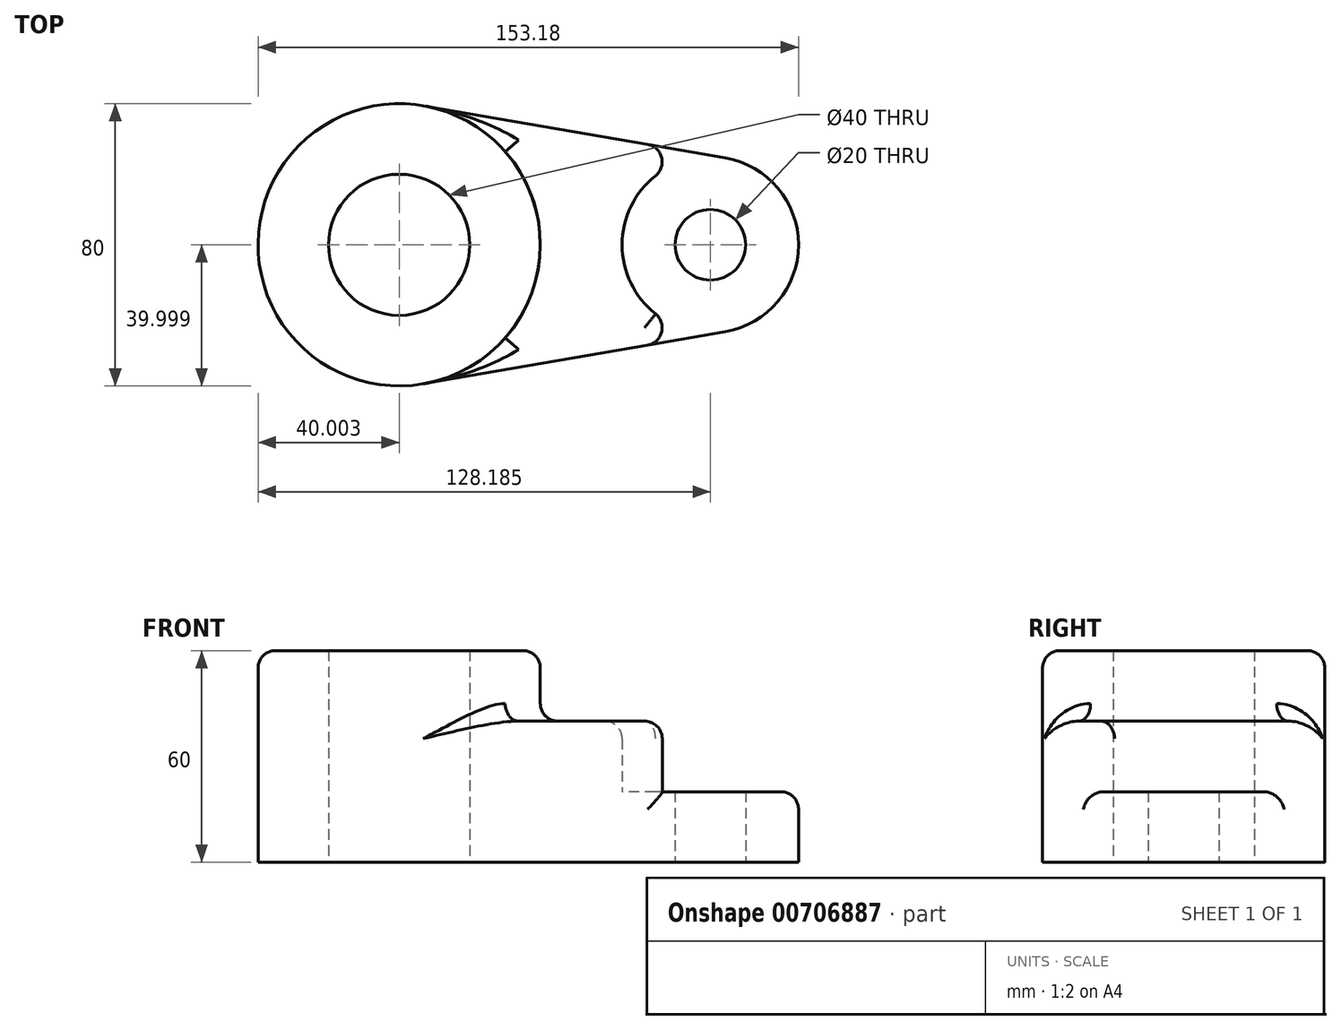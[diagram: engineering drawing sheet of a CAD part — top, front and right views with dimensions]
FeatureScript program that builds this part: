
annotation { "Feature Type Name" : "Feature", "Feature Type Description" : "" }
export const myFeature = defineFeature(function(context is Context, id is Id, definition is map)
    precondition{}
    {
        {
            var Q0;
            Q0=qCreatedBy(makeId("Top.planeOp"),FACE);
            var sketch = newSketch(context, id + "F0", { "sketchPlane" : qUnion([Q0])});
            skCircle(sketch, "E0", {"center": v(-39.4, 19.58) * mm, "radius": 40 * mm});
            skCircle(sketch, "E1", {"center": v(-39.4, 19.58) * mm, "radius": 20 * mm});
            skCircle(sketch, "E2", {"center": v(48.77, 19.58) * mm, "radius": 10 * mm});
            skCircle(sketch, "E3", {"center": v(48.77, 19.58) * mm, "radius": 25 * mm});
            skLineSegment(sketch, "E4", {"start": v(-32.6, 59) * mm, "end": v(53.03, 44.21) * mm});
            skLineSegment(sketch, "E5", {"start": v(-32.6, -19.84) * mm, "end": v(53.03, -5.06) * mm});
            skSolve(sketch);
        }
        {
            var Q0;
            Q0=makeQuery(id+"F0.imprint","IMPRINT",FACE,{"disambiguationData":[TD([[makeQuery(id+"F0.imprint","IMPRINT",EDGE,{"derivedFrom":sQuery(id+"F0.wireOp",EDGE,"E1")}),-1.0]])]});
            extrude(context, id + "F1", {"entities" : qUnion([Q0]), "depth" : 60 * mm, "offsetDistance" : 25 * mm});
        }
        {
            var Q0;
            {var subQ0=sQuery(id+"F0.wireOp",EDGE,"E4");Q0=makeQuery(id+"F0.imprint","IMPRINT",FACE,{"disambiguationData":[TD([[makeQuery(id+"F0.imprint","IMPRINT",EDGE,{"derivedFrom":subQ0}),-1.0]])]});}
            extrude(context, id + "F2", {"entities" : qUnion([Q0]), "operationType" : NewBodyOperationType.ADD, "depth" : 40 * mm, "offsetDistance" : 25 * mm});
        }
        {
            var Q0;
            Q0=makeQuery(id+"F0.imprint","IMPRINT",FACE,{"disambiguationData":[TD([[makeQuery(id+"F0.imprint","IMPRINT",EDGE,{"derivedFrom":sQuery(id+"F0.wireOp",EDGE,"E2")}),-1.0]])]});
            extrude(context, id + "F3", {"entities" : qUnion([Q0]), "operationType" : NewBodyOperationType.ADD, "depth" : 20 * mm, "offsetDistance" : 25 * mm});
        }
        {
            var Q0;
            Q0=makeQuery(id+"F1.opExtrude","CAP_EDGE",EDGE,{"disambiguationData":[OSD([sQuery(id+"F0.wireOp",EDGE,"E0")])],"isStart":false});
            var Q1;
            Q1=makeQuery(id+"F2.opExtrude","CAP_FACE",FACE,{"disambiguationData":[OSD([sQuery(id+"F0.wireOp",EDGE,"E0"),sQuery(id+"F0.wireOp",EDGE,"E3"),sQuery(id+"F0.wireOp",EDGE,"E4"),sQuery(id+"F0.wireOp",EDGE,"E5")])],"isStart":false});
            var Q2;
            {var subQ0=sQuery(id+"F0.wireOp",EDGE,"E3");var subQ1=sQuery(id+"F0.wireOp",EDGE,"E4");Q2=makeQuery(id+"F3.boolean.opBoolean","SPLIT",EDGE,{"disambiguationData":[topologyDisambiguationEdgeConnected([makeQuery(id+"F2.opExtrude","SWEPT_FACE",FACE,{"disambiguationData":[OSD([subQ0])]})])],"derivedFrom":makeQuery(id+"F2.opExtrude","SWEPT_EDGE",EDGE,{"disambiguationData":[OSD([subQ0,subQ1])]})});}
            var Q3;
            {var subQ0=sQuery(id+"F0.wireOp",EDGE,"E3");var subQ1=sQuery(id+"F0.wireOp",EDGE,"E5");Q3=makeQuery(id+"F3.boolean.opBoolean","SPLIT",EDGE,{"disambiguationData":[topologyDisambiguationEdgeConnected([makeQuery(id+"F2.opExtrude","SWEPT_FACE",FACE,{"disambiguationData":[OSD([subQ0])]})])],"derivedFrom":makeQuery(id+"F2.opExtrude","SWEPT_EDGE",EDGE,{"disambiguationData":[OSD([subQ0,subQ1])]})});}
            var Q4;
            Q4=makeQuery(id+"F2.opExtrude","CAP_EDGE",EDGE,{"disambiguationData":[OSD([sQuery(id+"F0.wireOp",EDGE,"E5")])],"isStart":false});
            fillet(context, id + "F4", {"entities" : qUnion([Q0, Q1, Q2, Q3, Q4]), "radius" : 5 * mm, "tangentPropagation" : true, "allowEdgeOverflow" : false});
        }
        {
            var Q0;
            {var subQ0=sQuery(id+"F0.wireOp",EDGE,"E3");Q0=makeQuery(id+"F3.boolean.opBoolean","SPLIT",EDGE,{"disambiguationData":[topologyDisambiguationEdgeConnected([makeQuery(id+"F3.opExtrude","SWEPT_FACE",FACE,{"disambiguationData":[OSD([subQ0])]})])],"derivedFrom":makeQuery(id+"F3.opExtrude","CAP_EDGE",EDGE,{"disambiguationData":[OSD([subQ0])],"isStart":false})});}
            fillet(context, id + "F5", {"entities" : qUnion([Q0]), "radius" : 5 * mm, "tangentPropagation" : true, "allowEdgeOverflow" : false});
        }
    });
